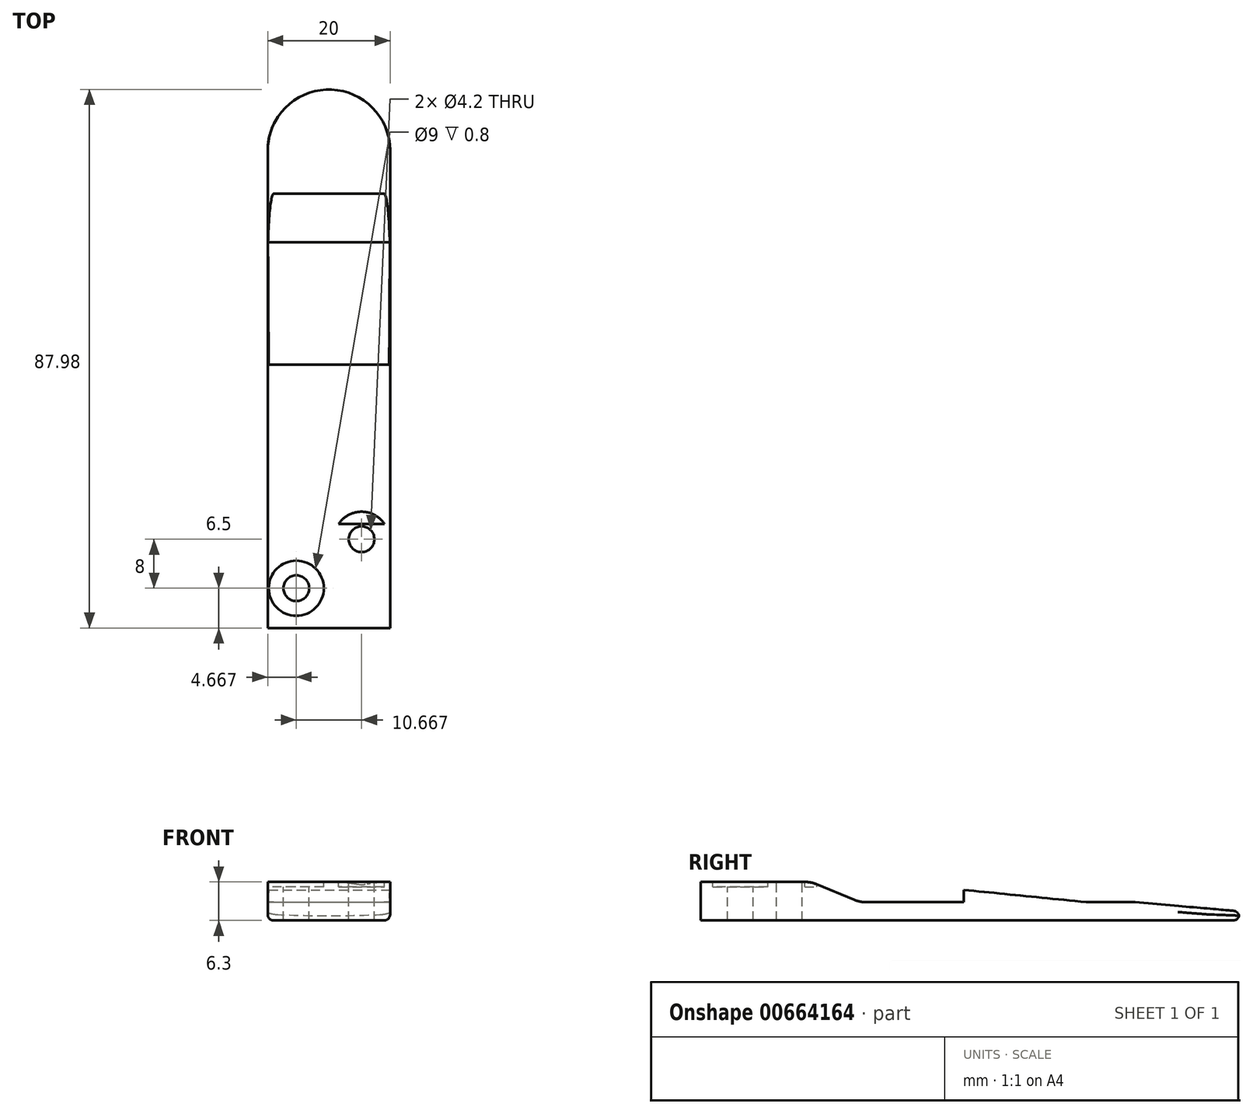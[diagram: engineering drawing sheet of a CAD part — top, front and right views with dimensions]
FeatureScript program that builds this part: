
annotation { "Feature Type Name" : "Feature", "Feature Type Description" : "" }
export const myFeature = defineFeature(function(context is Context, id is Id, definition is map)
    precondition{}
    {
        {
            var Q0;
            Q0=qCreatedBy(makeId("Top.planeOp"),FACE);
            var sketch = newSketch(context, id + "F0", { "sketchPlane" : qUnion([Q0])});
            skLineSegment(sketch, "E0.bottom", {"start": v(10, -37.5) * mm, "end": v(-10, -37.5) * mm});
            skLineSegment(sketch, "E0.top", {"start": v(10, 37.5) * mm, "end": v(-10, 37.5) * mm});
            skLineSegment(sketch, "E0.left", {"start": v(10, -37.5) * mm, "end": v(10, 37.5) * mm});
            skLineSegment(sketch, "E0.right", {"start": v(-10, -37.5) * mm, "end": v(-10, 37.5) * mm});
            skPoint(sketch, "E0.middle", {"position": v(0, 0) * mm});
            skSolve(sketch);
        }
        {
            var Q0;
            Q0=makeQuery(id+"F0.imprint","IMPRINT",FACE,{"disambiguationData":[TD([[makeQuery(id+"F0.imprint","IMPRINT",EDGE,{"derivedFrom":sQuery(id+"F0.wireOp",EDGE,"E0.bottom")}),-1.0]])]});
            extrude(context, id + "F1", {"entities" : qUnion([Q0]), "depth" : 3 * mm, "offsetDistance" : 25 * mm});
        }
        {
            var Q0;
            Q0=makeQuery(id+"F1.opExtrude","CAP_FACE",FACE,{"disambiguationData":[OSD([sQuery(id+"F0.wireOp",EDGE,"E0.bottom"),sQuery(id+"F0.wireOp",EDGE,"E0.top"),sQuery(id+"F0.wireOp",EDGE,"E0.left"),sQuery(id+"F0.wireOp",EDGE,"E0.right")])],"isStart":false});
            var sketch = newSketch(context, id + "F2", { "sketchPlane" : qUnion([Q0])});
            skLineSegment(sketch, "E1.bottom", {"start": v(-10, -37.5) * mm, "end": v(10, -37.5) * mm});
            skLineSegment(sketch, "E1.top", {"start": v(-10, -22.5) * mm, "end": v(10, -22.5) * mm});
            skLineSegment(sketch, "E1.left", {"start": v(-10, -37.5) * mm, "end": v(-10, -22.5) * mm});
            skLineSegment(sketch, "E1.right", {"start": v(10, -37.5) * mm, "end": v(10, -22.5) * mm});
            skSolve(sketch);
        }
        {
            var Q0;
            Q0=makeQuery(id+"F2.imprint","IMPRINT",FACE,{"disambiguationData":[TD([[makeQuery(id+"F2.imprint","IMPRINT",EDGE,{"derivedFrom":sQuery(id+"F2.wireOp",EDGE,"E1.bottom")}),-1.0]])]});
            extrude(context, id + "F3", {"entities" : qUnion([Q0]), "operationType" : NewBodyOperationType.ADD, "depth" : 3.3 * mm, "offsetDistance" : 25 * mm});
        }
        {
            var Q0;
            Q0=makeQuery(id+"F3.opExtrude","CAP_FACE",FACE,{"disambiguationData":[OSD([sQuery(id+"F2.wireOp",EDGE,"E1.bottom"),sQuery(id+"F2.wireOp",EDGE,"E1.top"),sQuery(id+"F2.wireOp",EDGE,"E1.left"),sQuery(id+"F2.wireOp",EDGE,"E1.right")])],"isStart":false});
            var sketch = newSketch(context, id + "F4", { "sketchPlane" : qUnion([Q0])});
            skCircle(sketch, "E2", {"center": v(-5.33, -34) * mm, "radius": 2.1 * mm});
            skCircle(sketch, "E3", {"center": v(5.33, -26) * mm, "radius": 2.1 * mm});
            skLineSegment(sketch, "E4", {"start": v(-10, -37.5) * mm, "end": v(10, -22.5) * mm, "construction": true});
            skSolve(sketch);
        }
        {
            var Q0;
            Q0=makeQuery(id+"F4.imprint","IMPRINT",FACE,{"disambiguationData":[TD([[makeQuery(id+"F4.imprint","IMPRINT",EDGE,{"derivedFrom":sQuery(id+"F4.wireOp",EDGE,"E3")}),1.0]])]});
            var Q1;
            Q1=makeQuery(id+"F4.imprint","IMPRINT",FACE,{"disambiguationData":[TD([[makeQuery(id+"F4.imprint","IMPRINT",EDGE,{"derivedFrom":sQuery(id+"F4.wireOp",EDGE,"E2")}),1.0]])]});
            extrude(context, id + "F5", {"entities" : qUnion([Q0, Q1]), "operationType" : NewBodyOperationType.REMOVE, "endBound" : BoundingType.THROUGH_ALL, "oppositeDirection" : true, "depth" : 25 * mm, "offsetDistance" : 25 * mm});
        }
        {
            var Q0;
            Q0=makeQuery(id+"F3.boolean.opBoolean","MERGE",FACE,{"derivedFrom":[makeQuery(id+"F1.opExtrude","SWEPT_FACE",FACE,{"disambiguationData":[OSD([sQuery(id+"F0.wireOp",EDGE,"E0.left")])]}),makeQuery(id+"F3.opExtrude","SWEPT_FACE",FACE,{"disambiguationData":[OSD([sQuery(id+"F2.wireOp",EDGE,"E1.right")])]})]});
            var sketch = newSketch(context, id + "F6", { "sketchPlane" : qUnion([Q0])});
            skLineSegment(sketch, "E5", {"start": v(2.5, 3) * mm, "end": v(2.5, 5) * mm});
            skLineSegment(sketch, "E6", {"start": v(2.5, 5) * mm, "end": v(22.5, 3) * mm});
            skLineSegment(sketch, "E7", {"start": v(22.5, 3) * mm, "end": v(2.5, 3) * mm});
            skLineSegment(sketch, "E8", {"start": v(-22.5, 6.3) * mm, "end": v(-14.5, 3) * mm});
            skSolve(sketch);
        }
        {
            var Q0;
            {var subQ0=sQuery(id+"F6.wireOp",EDGE,"CUDEGYpU-eG1w-oumi-qohX-08oMIDjLycTP");var subQ1=sQuery(id+"F6.wireOp",EDGE,"ysbfpdWN-y0Lm-AFJ7-kTbX-VYVF95nyCQNp");var subQ2=makeQuery(id+"F6.imprint","INTERSECT",VERTEX,{"derivedFrom":[subQ1,subQ0]});Q0=makeQuery(id+"F6.imprint","IMPRINT",FACE,{"disambiguationData":[TD([[makeQuery(id+"F6.imprint","IMPRINT",EDGE,{"disambiguationData":[TD([[subQ2,1.0]])],"derivedFrom":subQ1}),-1.0]])]});}
            var Q1;
            Q1=makeQuery(id+"F6.imprint","IMPRINT",FACE,{"disambiguationData":[TD([[makeQuery(id+"F6.imprint","IMPRINT",EDGE,{"derivedFrom":sQuery(id+"F6.wireOp",EDGE,"E5")}),-1.0]])]});
            var Q2;
            {var subQ0=sQuery(id+"F6.wireOp",EDGE,"E8");Q2=makeQuery(id+"F6.imprint","IMPRINT",FACE,{"disambiguationData":[TD([[makeQuery(id+"F6.imprint","IMPRINT",EDGE,{"derivedFrom":subQ0}),-1.0]])]});}
            var Q3;
            Q3=makeQuery(id+"F3.boolean.opBoolean","MERGE",FACE,{"derivedFrom":[makeQuery(id+"F1.opExtrude","SWEPT_FACE",FACE,{"disambiguationData":[OSD([sQuery(id+"F0.wireOp",EDGE,"E0.right")])]}),makeQuery(id+"F3.opExtrude","SWEPT_FACE",FACE,{"disambiguationData":[OSD([sQuery(id+"F2.wireOp",EDGE,"E1.left")])]})]});
            extrude(context, id + "F7", {"entities" : qUnion([Q0, Q1, Q2]), "operationType" : NewBodyOperationType.ADD, "endBound" : BoundingType.UP_TO_SURFACE, "oppositeDirection" : true, "depth" : 25 * mm, "endBoundEntityFace" : qUnion([Q3]), "offsetDistance" : 25 * mm});
        }
        {
            var Q0;
            Q0=makeQuery(id+"F1.opExtrude","CAP_FACE",FACE,{"disambiguationData":[OSD([sQuery(id+"F0.wireOp",EDGE,"E0.bottom"),sQuery(id+"F0.wireOp",EDGE,"E0.top"),sQuery(id+"F0.wireOp",EDGE,"E0.left"),sQuery(id+"F0.wireOp",EDGE,"E0.right")])],"isStart":true});
            var sketch = newSketch(context, id + "F8", { "sketchPlane" : qUnion([Q0])});
            skCircle(sketch, "E9", {"center": v(0, -37.5) * mm, "radius": 10 * mm});
            skSolve(sketch);
        }
        {
            var Q0;
            {var subQ1=makeQuery(id+"F1.opExtrude","CAP_EDGE",EDGE,{"disambiguationData":[OSD([sQuery(id+"F0.wireOp",EDGE,"E0.top")])],"isStart":true});Q0=makeQuery(id+"F8.imprint","IMPRINT",FACE,{"disambiguationData":[TD([[makeQuery(id+"F8.imprint","IMPRINT",EDGE,{"derivedFrom":subQ1}),1.0]])]});}
            var Q1;
            {var subQ0=sQuery(id+"F0.wireOp",EDGE,"E0.right");var subQ1=sQuery(id+"F0.wireOp",EDGE,"E0.left");var subQ2=sQuery(id+"F0.wireOp",EDGE,"E0.top");Q1=makeQuery(id+"F7.boolean.opBoolean","SPLIT",FACE,{"disambiguationData":[TD([makeQuery(id+"F1.opExtrude","SWEPT_FACE",FACE,{"disambiguationData":[OSD([subQ2])]})])],"derivedFrom":makeQuery(id+"F1.opExtrude","CAP_FACE",FACE,{"disambiguationData":[OSD([sQuery(id+"F0.wireOp",EDGE,"E0.bottom"),subQ2,subQ1,subQ0])],"isStart":false})});}
            extrude(context, id + "F9", {"entities" : qUnion([Q0]), "operationType" : NewBodyOperationType.ADD, "endBound" : BoundingType.UP_TO_SURFACE, "oppositeDirection" : true, "depth" : 25 * mm, "endBoundEntityFace" : qUnion([Q1]), "offsetDistance" : 25 * mm});
        }
        {
            var Q0;
            {var subQ0=sQuery(id+"F2.wireOp",EDGE,"E1.top");Q0=makeQuery(id+"F7.boolean.opBoolean","MERGE",EDGE,{"derivedFrom":[makeQuery(id+"F3.opExtrude","CAP_EDGE",EDGE,{"disambiguationData":[OSD([subQ0])],"isStart":false}),makeQuery(id+"F7.opExtrude","SWEPT_EDGE",EDGE,{"disambiguationData":[OSD([sQuery(id+"F0.wireOp",EDGE,"E0.left"),subQ0,sQuery(id+"F2.wireOp",EDGE,"E1.right"),sQuery(id+"F6.wireOp",EDGE,"E8")])]})]});}
            var Q1;
            Q1=makeQuery(id+"F7.opExtrude","SWEPT_EDGE",EDGE,{"disambiguationData":[OSD([sQuery(id+"F0.wireOp",EDGE,"E0.left"),sQuery(id+"F6.wireOp",EDGE,"E8")])]});
            var Q2;
            Q2=makeQuery(id+"F7.opExtrude","SWEPT_EDGE",EDGE,{"disambiguationData":[OSD([sQuery(id+"F0.wireOp",EDGE,"E0.left"),sQuery(id+"F6.wireOp",EDGE,"E6"),sQuery(id+"F6.wireOp",EDGE,"E7")])]});
            fillet(context, id + "F10", {"entities" : qUnion([Q0, Q1, Q2]), "radius" : 5 * mm, "tangentPropagation" : true, "allowEdgeOverflow" : false});
        }
        {
            var Q0;
            {var subQ0=sQuery(id+"F2.wireOp",EDGE,"E1.right");var subQ1=sQuery(id+"F0.wireOp",EDGE,"E0.left");Q0=makeQuery(id+"F7.boolean.opBoolean","MERGE",FACE,{"derivedFrom":[makeQuery(id+"F3.boolean.opBoolean","MERGE",FACE,{"derivedFrom":[makeQuery(id+"F1.opExtrude","SWEPT_FACE",FACE,{"disambiguationData":[OSD([subQ1])]}),makeQuery(id+"F3.opExtrude","SWEPT_FACE",FACE,{"disambiguationData":[OSD([subQ0])]})]}),makeQuery(id+"F7.opExtrude","CAP_FACE",FACE,{"disambiguationData":[OSD([sQuery(id+"F6.wireOp",EDGE,"E5"),sQuery(id+"F6.wireOp",EDGE,"E6"),sQuery(id+"F6.wireOp",EDGE,"E7")])],"isStart":true}),makeQuery(id+"F7.opExtrude","CAP_FACE",FACE,{"disambiguationData":[OSD([subQ1,sQuery(id+"F2.wireOp",EDGE,"E1.top"),subQ0,sQuery(id+"F6.wireOp",EDGE,"E8")])],"isStart":true})]});}
            var sketch = newSketch(context, id + "F11", { "sketchPlane" : qUnion([Q0])});
            skLineSegment(sketch, "E10", {"start": v(30.5, 3) * mm, "end": v(47.5, 3) * mm});
            skLineSegment(sketch, "E11", {"start": v(47.5, 3) * mm, "end": v(47.5, 1.5) * mm});
            skLineSegment(sketch, "E12", {"start": v(47.5, 1.5) * mm, "end": v(30.5, 3) * mm});
            skSolve(sketch);
        }
        {
            var Q0;
            {var subQ5=sQuery(id+"F11.wireOp",EDGE,"E11");Q0=makeQuery(id+"F11.imprint","IMPRINT",FACE,{"disambiguationData":[TD([[makeQuery(id+"F11.imprint","IMPRINT",EDGE,{"derivedFrom":subQ5}),-1.0]])]});}
            var Q1;
            {var subQ0=sQuery(id+"F11.wireOp",EDGE,"E10");var subQ1=sQuery(id+"F0.wireOp",EDGE,"E0.left");var subQ2=sQuery(id+"F0.wireOp",EDGE,"E0.top");var subQ3=makeQuery(id+"F9.boolean.opBoolean","MERGE",EDGE,{"derivedFrom":[makeQuery(id+"F1.opExtrude","SWEPT_EDGE",EDGE,{"disambiguationData":[OSD([subQ2,subQ1])]}),makeQuery(id+"F9.opExtrude","SWEPT_EDGE",EDGE,{"disambiguationData":[OSD([subQ2,subQ1,sQuery(id+"F8.wireOp",EDGE,"E9")])]})]});var subQ4=makeQuery(id+"F11.imprint","INTERSECT",VERTEX,{"derivedFrom":[subQ3,subQ0]});Q1=makeQuery(id+"F11.imprint","IMPRINT",FACE,{"disambiguationData":[TD([[makeQuery(id+"F11.imprint","IMPRINT",EDGE,{"disambiguationData":[TD([[subQ4,-1.0]])],"derivedFrom":subQ3}),-1.0]])]});}
            var Q2;
            Q2=makeQuery(id+"F7.boolean.opBoolean","MERGE",FACE,{"derivedFrom":[makeQuery(id+"F3.boolean.opBoolean","MERGE",FACE,{"derivedFrom":[makeQuery(id+"F1.opExtrude","SWEPT_FACE",FACE,{"disambiguationData":[OSD([sQuery(id+"F0.wireOp",EDGE,"E0.right")])]}),makeQuery(id+"F3.opExtrude","SWEPT_FACE",FACE,{"disambiguationData":[OSD([sQuery(id+"F2.wireOp",EDGE,"E1.left")])]})]}),makeQuery(id+"F7.opExtrude","CAP_FACE",FACE,{"disambiguationData":[OSD([sQuery(id+"F6.wireOp",EDGE,"E5"),sQuery(id+"F6.wireOp",EDGE,"E6"),sQuery(id+"F6.wireOp",EDGE,"E7")])],"isStart":false}),makeQuery(id+"F7.opExtrude","CAP_FACE",FACE,{"disambiguationData":[OSD([sQuery(id+"F0.wireOp",EDGE,"E0.left"),sQuery(id+"F2.wireOp",EDGE,"E1.top"),sQuery(id+"F2.wireOp",EDGE,"E1.right"),sQuery(id+"F6.wireOp",EDGE,"E8")])],"isStart":false})]});
            extrude(context, id + "F12", {"entities" : qUnion([Q0, Q1]), "operationType" : NewBodyOperationType.REMOVE, "endBound" : BoundingType.UP_TO_SURFACE, "oppositeDirection" : true, "depth" : 25 * mm, "endBoundEntityFace" : qUnion([Q2]), "offsetDistance" : 25 * mm});
        }
        {
            var Q0;
            Q0=makeQuery(id+"F3.boolean.opBoolean","MERGE",FACE,{"derivedFrom":[makeQuery(id+"F1.opExtrude","SWEPT_FACE",FACE,{"disambiguationData":[OSD([sQuery(id+"F0.wireOp",EDGE,"E0.bottom")])]}),makeQuery(id+"F3.opExtrude","SWEPT_FACE",FACE,{"disambiguationData":[OSD([sQuery(id+"F2.wireOp",EDGE,"E1.bottom")])]})]});
            var sketch = newSketch(context, id + "F13", { "sketchPlane" : qUnion([Q0])});
            skLineSegment(sketch, "E13.bottom", {"start": v(-10, 0) * mm, "end": v(10, 0) * mm});
            skLineSegment(sketch, "E13.top", {"start": v(-10, 6.3) * mm, "end": v(10, 6.3) * mm});
            skLineSegment(sketch, "E13.left", {"start": v(-10, 0) * mm, "end": v(-10, 6.3) * mm});
            skLineSegment(sketch, "E13.right", {"start": v(10, 0) * mm, "end": v(10, 6.3) * mm});
            skSolve(sketch);
        }
        {
            var Q0;
            Q0=makeQuery(id+"F13.imprint","IMPRINT",FACE,{"disambiguationData":[TD([[makeQuery(id+"F13.imprint","IMPRINT",EDGE,{"derivedFrom":sQuery(id+"F13.wireOp",EDGE,"E13.bottom")}),-1.0]])]});
            extrude(context, id + "F14", {"entities" : qUnion([Q0]), "operationType" : NewBodyOperationType.ADD, "depth" : 3 * mm, "offsetDistance" : 25 * mm});
        }
        {
            var Q0;
            Q0=makeQuery(id+"F3.opExtrude","CAP_FACE",FACE,{"disambiguationData":[OSD([sQuery(id+"F2.wireOp",EDGE,"E1.bottom"),sQuery(id+"F2.wireOp",EDGE,"E1.top"),sQuery(id+"F2.wireOp",EDGE,"E1.left"),sQuery(id+"F2.wireOp",EDGE,"E1.right")])],"isStart":false});
            var sketch = newSketch(context, id + "F15", { "sketchPlane" : qUnion([Q0])});
            skCircle(sketch, "E14", {"center": v(5.33, -26) * mm, "radius": 4.5 * mm});
            skCircle(sketch, "E15", {"center": v(-5.33, -34) * mm, "radius": 4.5 * mm});
            skSolve(sketch);
        }
        {
            var Q0;
            Q0=makeQuery(id+"F15.imprint","IMPRINT",FACE,{"disambiguationData":[TD([[makeQuery(id+"F15.imprint","IMPRINT",EDGE,{"derivedFrom":sQuery(id+"F15.wireOp",EDGE,"E15")}),1.0]])]});
            var Q1;
            Q1=makeQuery(id+"F15.imprint","IMPRINT",FACE,{"disambiguationData":[TD([[makeQuery(id+"F15.imprint","IMPRINT",EDGE,{"derivedFrom":makeQuery(id+"F5.boolean.opBoolean","COPY",EDGE,{"derivedFrom":makeQuery(id+"F5.opExtrude","CAP_EDGE",EDGE,{"disambiguationData":[OSD([sQuery(id+"F4.wireOp",EDGE,"E3")])],"isStart":true})})}),-1.0]])]});
            var Q2;
            {var subQ0=sQuery(id+"F15.wireOp",EDGE,"E14");var subQ1=sQuery(id+"F2.wireOp",EDGE,"E1.right");var subQ2=sQuery(id+"F2.wireOp",EDGE,"E1.top");var subQ3=makeQuery(id+"F10.opFillet","BLEND_EDGE",EDGE,{"blendedFrom":[makeQuery(id+"F7.boolean.opBoolean","MERGE",EDGE,{"derivedFrom":[makeQuery(id+"F3.opExtrude","CAP_EDGE",EDGE,{"disambiguationData":[OSD([subQ2])],"isStart":false}),makeQuery(id+"F7.opExtrude","SWEPT_EDGE",EDGE,{"disambiguationData":[OSD([sQuery(id+"F0.wireOp",EDGE,"E0.left"),subQ2,subQ1,sQuery(id+"F6.wireOp",EDGE,"E8")])]})]}),makeQuery(id+"F3.opExtrude","CAP_FACE",FACE,{"disambiguationData":[OSD([sQuery(id+"F2.wireOp",EDGE,"E1.bottom"),subQ2,sQuery(id+"F2.wireOp",EDGE,"E1.left"),subQ1])],"isStart":false})],"blendedInto":[makeQuery(id+"F3.opExtrude","CAP_FACE",FACE,{"disambiguationData":[OSD([sQuery(id+"F2.wireOp",EDGE,"E1.bottom"),subQ2,sQuery(id+"F2.wireOp",EDGE,"E1.left"),subQ1])],"isStart":false})]});var subQ4=makeQuery(id+"F15.imprint","INTERSECT",VERTEX,{"disambiguationData":[OD(0.0)],"derivedFrom":[subQ3,subQ0]});Q2=makeQuery(id+"F15.imprint","IMPRINT",FACE,{"disambiguationData":[TD([[makeQuery(id+"F15.imprint","IMPRINT",EDGE,{"disambiguationData":[TD([[subQ4,-1.0]])],"derivedFrom":subQ0}),1.0]])]});}
            extrude(context, id + "F16", {"entities" : qUnion([Q0, Q1, Q2]), "operationType" : NewBodyOperationType.REMOVE, "oppositeDirection" : true, "depth" : 0.8 * mm, "offsetDistance" : 25 * mm});
        }
        {
            var Q0;
            Q0=makeQuery(id+"F12.boolean.opBoolean","INTERSECT",EDGE,{"derivedFrom":[makeQuery(id+"F9.opExtrude","SWEPT_FACE",FACE,{"disambiguationData":[OSD([sQuery(id+"F8.wireOp",EDGE,"E9")])]}),makeQuery(id+"F12.opExtrude","SWEPT_FACE",FACE,{"disambiguationData":[OSD([sQuery(id+"F11.wireOp",EDGE,"E12")])]})]});
            var Q1;
            Q1=makeQuery(id+"F9.opExtrude","CAP_EDGE",EDGE,{"disambiguationData":[OSD([sQuery(id+"F8.wireOp",EDGE,"E9")])],"isStart":true});
            fillet(context, id + "F17", {"entities" : qUnion([Q0, Q1]), "radius" : 1 * mm, "tangentPropagation" : true, "allowEdgeOverflow" : false});
        }
    });
